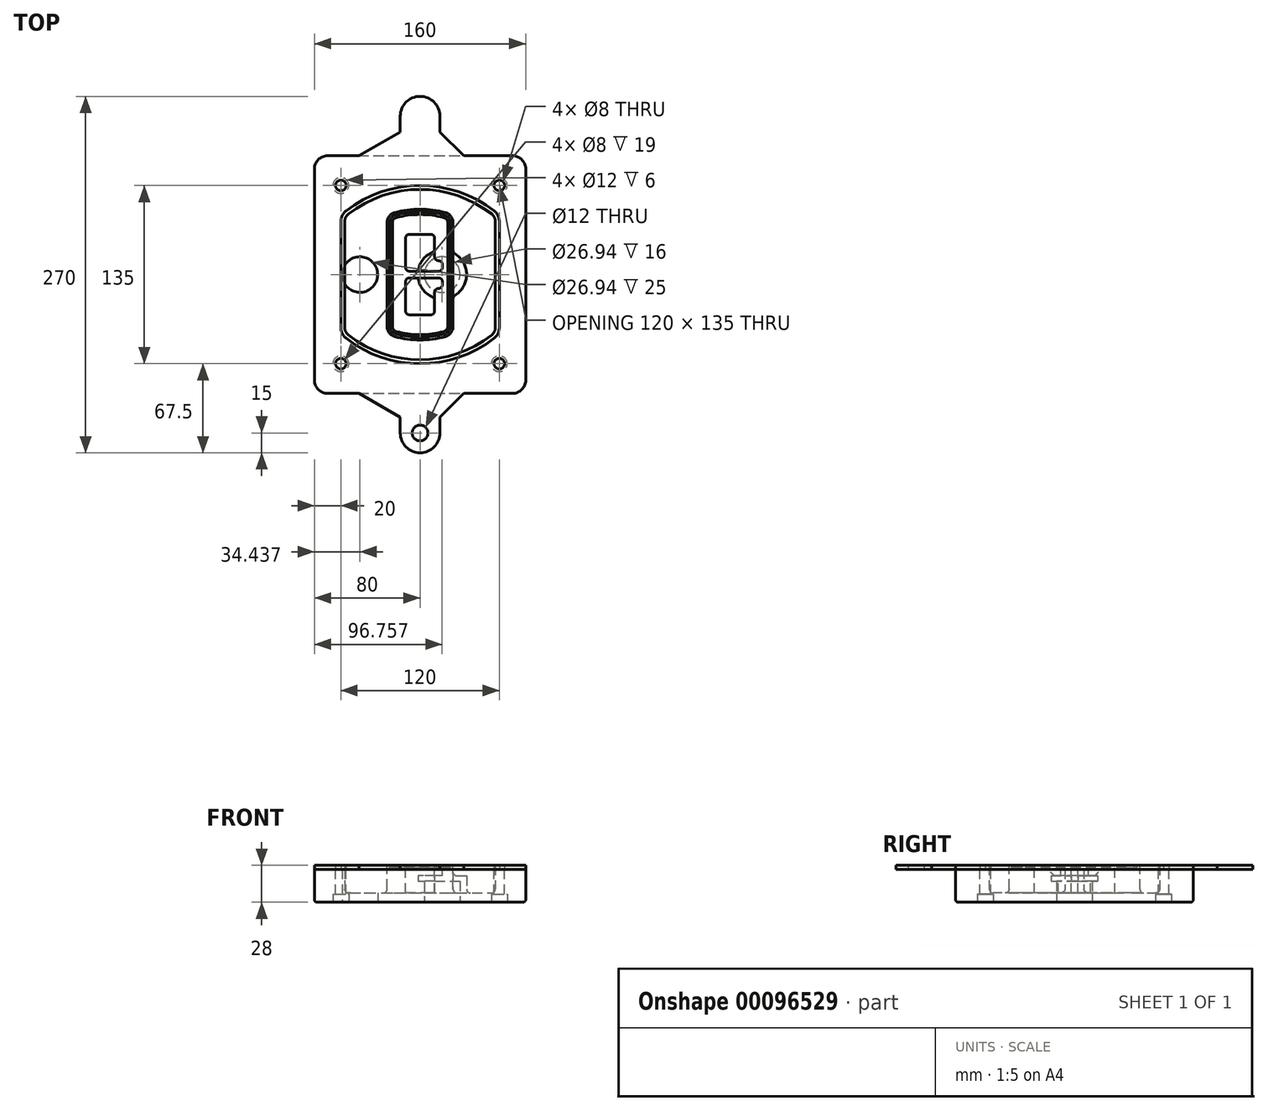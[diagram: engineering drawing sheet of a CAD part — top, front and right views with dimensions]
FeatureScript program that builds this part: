
annotation { "Feature Type Name" : "Feature", "Feature Type Description" : "" }
export const myFeature = defineFeature(function(context is Context, id is Id, definition is map)
    precondition{}
    {
        {
            var Q0;
            Q0=qCreatedBy(makeId("Top.planeOp"),FACE);
            var sketch = newSketch(context, id + "F0", { "sketchPlane" : qUnion([Q0])});
            skPoint(sketch, "E0.rect.middle", {"position": v(0, 0) * mm});
            skLineSegment(sketch, "E1.bottom", {"start": v(-70, -90) * mm, "end": v(70, -90) * mm});
            skLineSegment(sketch, "E1.top", {"start": v(-70, 90) * mm, "end": v(70, 90) * mm});
            skLineSegment(sketch, "E1.left", {"start": v(-80, -80) * mm, "end": v(-80, 80) * mm});
            skLineSegment(sketch, "E1.right", {"start": v(80, -80) * mm, "end": v(80, 80) * mm});
            skLineSegment(sketch, "E2", {"start": v(-80, 90) * mm, "end": v(80, -90) * mm, "construction": true});
            skLineSegment(sketch, "E3", {"start": v(80, 90) * mm, "end": v(-80, -90) * mm, "construction": true});
            skCircle(sketch, "E4", {"center": v(-60, 67.5) * mm, "radius": 4 * mm});
            skCircle(sketch, "E5", {"center": v(60, 67.5) * mm, "radius": 4 * mm});
            skCircle(sketch, "E6", {"center": v(60, -67.5) * mm, "radius": 4 * mm});
            skCircle(sketch, "E7", {"center": v(-60, -67.5) * mm, "radius": 4 * mm});
            skLineSegment(sketch, "E8", {"start": v(-60, 67.5) * mm, "end": v(60, 67.5) * mm, "construction": true});
            skLineSegment(sketch, "E9", {"start": v(60, 67.5) * mm, "end": v(60, -67.5) * mm, "construction": true});
            skLineSegment(sketch, "E10", {"start": v(60, -67.5) * mm, "end": v(-60, -67.5) * mm, "construction": true});
            skLineSegment(sketch, "E11", {"start": v(-60, -67.5) * mm, "end": v(-60, 67.5) * mm, "construction": true});
            skLineSegment(sketch, "E12", {"start": v(-60, 40.3) * mm, "end": v(-60, -40.3) * mm});
            skLineSegment(sketch, "E13", {"start": v(60, 40.3) * mm, "end": v(60, -40.3) * mm});
            skArc(sketch, "E14", {"start": v(56.15, 48.18) * mm, "mid": v(0, 67.5) * mm, "end": v(-56.15, 48.18) * mm});
            skArc(sketch, "E15", {"start": v(-56.15, -48.18) * mm, "mid": v(0, -67.5) * mm, "end": v(56.15, -48.18) * mm});
            skLineSegment(sketch, "E16", {"start": v(-60, 0) * mm, "end": v(60, 0) * mm, "construction": true});
            skPoint(sketch, "E17.visualSharp", {"position": v(-60, -45) * mm});
            skArc(sketch, "E17.filletArc", {"start": v(-60, -40.3) * mm, "mid": v(-58.99, -44.68) * mm, "end": v(-56.15, -48.18) * mm});
            skPoint(sketch, "E18.visualSharp", {"position": v(-60, 45) * mm});
            skArc(sketch, "E18.filletArc", {"start": v(-56.15, 48.18) * mm, "mid": v(-58.99, 44.68) * mm, "end": v(-60, 40.3) * mm});
            skPoint(sketch, "E19.visualSharp", {"position": v(60, 45) * mm});
            skArc(sketch, "E19.filletArc", {"start": v(60, 40.3) * mm, "mid": v(58.99, 44.68) * mm, "end": v(56.15, 48.18) * mm});
            skPoint(sketch, "E20.visualSharp", {"position": v(60, -45) * mm});
            skArc(sketch, "E20.filletArc", {"start": v(56.15, -48.18) * mm, "mid": v(58.99, -44.68) * mm, "end": v(60, -40.3) * mm});
            skPoint(sketch, "E21.visualSharp", {"position": v(-80, 90) * mm});
            skArc(sketch, "E21.filletArc", {"start": v(-70, 90) * mm, "mid": v(-77.07, 87.07) * mm, "end": v(-80, 80) * mm});
            skPoint(sketch, "E22.visualSharp", {"position": v(80, 90) * mm});
            skArc(sketch, "E22.filletArc", {"start": v(80, 80) * mm, "mid": v(77.07, 87.07) * mm, "end": v(70, 90) * mm});
            skPoint(sketch, "E23.visualSharp", {"position": v(80, -90) * mm});
            skArc(sketch, "E23.filletArc", {"start": v(70, -90) * mm, "mid": v(77.07, -87.07) * mm, "end": v(80, -80) * mm});
            skPoint(sketch, "E24.visualSharp", {"position": v(-80, -90) * mm});
            skArc(sketch, "E24.filletArc", {"start": v(-80, -80) * mm, "mid": v(-77.07, -87.07) * mm, "end": v(-70, -90) * mm});
            skArc(sketch, "E25.0", {"start": v(57, 40.3) * mm, "mid": v(56.3, 43.36) * mm, "end": v(54.3, 45.81) * mm});
            skLineSegment(sketch, "E25.1", {"start": v(57, 40.3) * mm, "end": v(57, -40.3) * mm});
            skArc(sketch, "E25.2", {"start": v(54.3, -45.81) * mm, "mid": v(56.3, -43.36) * mm, "end": v(57, -40.3) * mm});
            skArc(sketch, "E25.3", {"start": v(-54.3, -45.81) * mm, "mid": v(0, -64.5) * mm, "end": v(54.3, -45.81) * mm});
            skArc(sketch, "E25.4", {"start": v(-57, -40.3) * mm, "mid": v(-56.3, -43.36) * mm, "end": v(-54.3, -45.81) * mm});
            skArc(sketch, "E25.5", {"start": v(54.3, 45.81) * mm, "mid": v(0, 64.5) * mm, "end": v(-54.3, 45.81) * mm});
            skLineSegment(sketch, "E25.6", {"start": v(-57, 40.3) * mm, "end": v(-57, -40.3) * mm});
            skArc(sketch, "E25.7", {"start": v(-54.3, 45.81) * mm, "mid": v(-56.3, 43.36) * mm, "end": v(-57, 40.3) * mm});
            skArc(sketch, "E26.0", {"start": v(-58.62, 51.33) * mm, "mid": v(-62.58, 46.43) * mm, "end": v(-64, 40.3) * mm});
            skArc(sketch, "E26.1", {"start": v(58.62, 51.33) * mm, "mid": v(0, 71.5) * mm, "end": v(-58.62, 51.33) * mm});
            skArc(sketch, "E26.2", {"start": v(64, 40.3) * mm, "mid": v(62.58, 46.43) * mm, "end": v(58.62, 51.33) * mm});
            skLineSegment(sketch, "E26.3", {"start": v(64, 40.3) * mm, "end": v(64, -40.3) * mm});
            skArc(sketch, "E26.4", {"start": v(58.62, -51.33) * mm, "mid": v(62.58, -46.43) * mm, "end": v(64, -40.3) * mm});
            skLineSegment(sketch, "E26.5", {"start": v(-64, 40.3) * mm, "end": v(-64, -40.3) * mm});
            skArc(sketch, "E26.6", {"start": v(-58.62, -51.33) * mm, "mid": v(0, -71.5) * mm, "end": v(58.62, -51.33) * mm});
            skArc(sketch, "E26.7", {"start": v(-64, -40.3) * mm, "mid": v(-62.58, -46.43) * mm, "end": v(-58.62, -51.33) * mm});
            skSolve(sketch);
        }
        {
            var Q0;
            Q0=makeQuery(id+"F0.imprint","IMPRINT",FACE,{"disambiguationData":[TD([[makeQuery(id+"F0.imprint","IMPRINT",EDGE,{"derivedFrom":sQuery(id+"F0.wireOp",EDGE,"E1.bottom")}),1.0]])]});
            var Q1;
            Q1=makeQuery(id+"F0.imprint","IMPRINT",FACE,{"disambiguationData":[TD([[makeQuery(id+"F0.imprint","IMPRINT",EDGE,{"derivedFrom":sQuery(id+"F0.wireOp",EDGE,"E12")}),1.0]])]});
            var Q2;
            Q2=makeQuery(id+"F0.imprint","IMPRINT",FACE,{"disambiguationData":[TD([[makeQuery(id+"F0.imprint","IMPRINT",EDGE,{"derivedFrom":sQuery(id+"F0.wireOp",EDGE,"E25.0")}),1.0]])]});
            var Q3;
            Q3=makeQuery(id+"F0.imprint","IMPRINT",FACE,{"disambiguationData":[TD([[makeQuery(id+"F0.imprint","IMPRINT",EDGE,{"derivedFrom":sQuery(id+"F0.wireOp",EDGE,"E12")}),-1.0]])]});
            extrude(context, id + "F1", {"entities" : qUnion([Q0, Q1, Q2, Q3]), "oppositeDirection" : true, "depth" : 25 * mm});
        }
        {
            var Q0;
            Q0=makeQuery(id+"F0.imprint","IMPRINT",FACE,{"disambiguationData":[TD([[makeQuery(id+"F0.imprint","IMPRINT",EDGE,{"derivedFrom":sQuery(id+"F0.wireOp",EDGE,"E12")}),1.0]])]});
            extrude(context, id + "F2", {"entities" : qUnion([Q0]), "operationType" : NewBodyOperationType.ADD, "depth" : 3 * mm});
        }
        {
            var Q0;
            Q0=makeQuery(id+"F0.imprint","IMPRINT",FACE,{"disambiguationData":[TD([[makeQuery(id+"F0.imprint","IMPRINT",EDGE,{"derivedFrom":sQuery(id+"F0.wireOp",EDGE,"E25.0")}),1.0]])]});
            extrude(context, id + "F3", {"entities" : qUnion([Q0]), "operationType" : NewBodyOperationType.REMOVE, "oppositeDirection" : true, "depth" : 18 * mm});
        }
        {
            var Q0;
            Q0=makeQuery(id+"F2.opExtrude","CAP_FACE",FACE,{"disambiguationData":[OSD([sQuery(id+"F0.wireOp",EDGE,"E12"),sQuery(id+"F0.wireOp",EDGE,"E13"),sQuery(id+"F0.wireOp",EDGE,"E14"),sQuery(id+"F0.wireOp",EDGE,"E15"),sQuery(id+"F0.wireOp",EDGE,"E17.filletArc"),sQuery(id+"F0.wireOp",EDGE,"E18.filletArc"),sQuery(id+"F0.wireOp",EDGE,"E19.filletArc"),sQuery(id+"F0.wireOp",EDGE,"E20.filletArc"),sQuery(id+"F0.wireOp",EDGE,"E25.0"),sQuery(id+"F0.wireOp",EDGE,"E25.1"),sQuery(id+"F0.wireOp",EDGE,"E25.2"),sQuery(id+"F0.wireOp",EDGE,"E25.3"),sQuery(id+"F0.wireOp",EDGE,"E25.4"),sQuery(id+"F0.wireOp",EDGE,"E25.5"),sQuery(id+"F0.wireOp",EDGE,"E25.6"),sQuery(id+"F0.wireOp",EDGE,"E25.7")])],"isStart":false});
            var sketch = newSketch(context, id + "F4", { "sketchPlane" : qUnion([Q0])});
            skArc(sketch, "E27.0", {"start": v(-19.08, -46.97) * mm, "mid": v(0, -49.5) * mm, "end": v(19.08, -46.97) * mm});
            skArc(sketch, "E28.0", {"start": v(19.08, 46.97) * mm, "mid": v(0, 49.5) * mm, "end": v(-19.08, 46.97) * mm});
            skLineSegment(sketch, "E29", {"start": v(-25, 39.25) * mm, "end": v(-25, -39.25) * mm});
            skLineSegment(sketch, "E30", {"start": v(25, 39.25) * mm, "end": v(25, -39.25) * mm});
            skLineSegment(sketch, "E31", {"start": v(-25, 45.1) * mm, "end": v(25, 45.1) * mm, "construction": true});
            skLineSegment(sketch, "E32", {"start": v(-25, -45.1) * mm, "end": v(25, -45.1) * mm, "construction": true});
            skPoint(sketch, "E33.visualSharp", {"position": v(-25, 45.1) * mm});
            skArc(sketch, "E33.filletArc", {"start": v(-19.08, 46.97) * mm, "mid": v(-23.35, 44.11) * mm, "end": v(-25, 39.25) * mm});
            skPoint(sketch, "E34.visualSharp", {"position": v(25, 45.1) * mm});
            skArc(sketch, "E34.filletArc", {"start": v(25, 39.25) * mm, "mid": v(23.35, 44.11) * mm, "end": v(19.08, 46.97) * mm});
            skPoint(sketch, "E35.visualSharp", {"position": v(25, -45.1) * mm});
            skArc(sketch, "E35.filletArc", {"start": v(19.08, -46.97) * mm, "mid": v(23.35, -44.11) * mm, "end": v(25, -39.25) * mm});
            skPoint(sketch, "E36.visualSharp", {"position": v(-25, -45.1) * mm});
            skArc(sketch, "E36.filletArc", {"start": v(-25, -39.25) * mm, "mid": v(-23.35, -44.11) * mm, "end": v(-19.08, -46.97) * mm});
            skArc(sketch, "E37.0", {"start": v(54.3, 45.81) * mm, "mid": v(0, 64.5) * mm, "end": v(-54.3, 45.81) * mm});
            skArc(sketch, "E37.1", {"start": v(-54.3, 45.81) * mm, "mid": v(-56.3, 43.36) * mm, "end": v(-57, 40.3) * mm});
            skLineSegment(sketch, "E37.2", {"start": v(-57, 40.3) * mm, "end": v(-57, -40.3) * mm});
            skArc(sketch, "E37.3", {"start": v(-57, -40.3) * mm, "mid": v(-56.3, -43.36) * mm, "end": v(-54.3, -45.81) * mm});
            skArc(sketch, "E37.4", {"start": v(-54.3, -45.81) * mm, "mid": v(0, -64.5) * mm, "end": v(54.3, -45.81) * mm});
            skArc(sketch, "E37.5", {"start": v(54.3, -45.81) * mm, "mid": v(56.3, -43.36) * mm, "end": v(57, -40.3) * mm});
            skLineSegment(sketch, "E37.6", {"start": v(57, 40.3) * mm, "end": v(57, -40.3) * mm});
            skArc(sketch, "E37.7", {"start": v(57, 40.3) * mm, "mid": v(56.3, 43.36) * mm, "end": v(54.3, 45.81) * mm});
            skLineSegment(sketch, "E38.0", {"start": v(23, 39.25) * mm, "end": v(23, -39.25) * mm});
            skArc(sketch, "E38.1", {"start": v(18.56, -45.04) * mm, "mid": v(21.76, -42.9) * mm, "end": v(23, -39.25) * mm});
            skArc(sketch, "E38.2", {"start": v(-18.56, -45.04) * mm, "mid": v(0, -47.5) * mm, "end": v(18.56, -45.04) * mm});
            skArc(sketch, "E38.3", {"start": v(-23, -39.25) * mm, "mid": v(-21.76, -42.9) * mm, "end": v(-18.56, -45.04) * mm});
            skLineSegment(sketch, "E38.4", {"start": v(-23, 39.25) * mm, "end": v(-23, -39.25) * mm});
            skArc(sketch, "E38.5", {"start": v(23, 39.25) * mm, "mid": v(21.76, 42.9) * mm, "end": v(18.56, 45.04) * mm});
            skArc(sketch, "E38.6", {"start": v(-18.56, 45.04) * mm, "mid": v(-21.76, 42.9) * mm, "end": v(-23, 39.25) * mm});
            skArc(sketch, "E38.7", {"start": v(18.56, 45.04) * mm, "mid": v(0, 47.5) * mm, "end": v(-18.56, 45.04) * mm});
            skArc(sketch, "E39.0", {"start": v(21, 39.25) * mm, "mid": v(20.18, 41.68) * mm, "end": v(18.04, 43.1) * mm});
            skLineSegment(sketch, "E39.1", {"start": v(21, 39.25) * mm, "end": v(21, -39.25) * mm});
            skArc(sketch, "E39.2", {"start": v(18.04, -43.1) * mm, "mid": v(20.18, -41.68) * mm, "end": v(21, -39.25) * mm});
            skArc(sketch, "E39.3", {"start": v(-18.04, -43.1) * mm, "mid": v(0, -45.5) * mm, "end": v(18.04, -43.1) * mm});
            skArc(sketch, "E39.4", {"start": v(-21, -39.25) * mm, "mid": v(-20.18, -41.68) * mm, "end": v(-18.04, -43.1) * mm});
            skArc(sketch, "E39.5", {"start": v(18.04, 43.1) * mm, "mid": v(0, 45.5) * mm, "end": v(-18.04, 43.1) * mm});
            skLineSegment(sketch, "E39.6", {"start": v(-21, 39.25) * mm, "end": v(-21, -39.25) * mm});
            skArc(sketch, "E39.7", {"start": v(-18.04, 43.1) * mm, "mid": v(-20.18, 41.68) * mm, "end": v(-21, 39.25) * mm});
            skLineSegment(sketch, "E40", {"start": v(-25, 0) * mm, "end": v(25, 0) * mm, "construction": true});
            skLineSegment(sketch, "E41", {"start": v(-11, 5.5) * mm, "end": v(-11, 27.5) * mm});
            skLineSegment(sketch, "E42", {"start": v(-8, 30.5) * mm, "end": v(8, 30.5) * mm});
            skLineSegment(sketch, "E43", {"start": v(11, 27.5) * mm, "end": v(11, 13.5) * mm});
            skLineSegment(sketch, "E44", {"start": v(14, 10.5) * mm, "end": v(14, 10.5) * mm});
            skLineSegment(sketch, "E45", {"start": v(17, 7.5) * mm, "end": v(17, 5.5) * mm});
            skLineSegment(sketch, "E46", {"start": v(14, 2.5) * mm, "end": v(-8, 2.5) * mm});
            skPoint(sketch, "E47.visualSharp", {"position": v(-11, 30.5) * mm});
            skArc(sketch, "E47.filletArc", {"start": v(-8, 30.5) * mm, "mid": v(-10.12, 29.62) * mm, "end": v(-11, 27.5) * mm});
            skPoint(sketch, "E48.visualSharp", {"position": v(11, 30.5) * mm});
            skArc(sketch, "E48.filletArc", {"start": v(11, 27.5) * mm, "mid": v(10.12, 29.62) * mm, "end": v(8, 30.5) * mm});
            skPoint(sketch, "E49.visualSharp", {"position": v(11, 10.5) * mm});
            skArc(sketch, "E49.filletArc", {"start": v(11, 13.5) * mm, "mid": v(11.88, 11.38) * mm, "end": v(14, 10.5) * mm});
            skPoint(sketch, "E50.visualSharp", {"position": v(17, 10.5) * mm});
            skArc(sketch, "E50.filletArc", {"start": v(17, 7.5) * mm, "mid": v(16.12, 9.62) * mm, "end": v(14, 10.5) * mm});
            skPoint(sketch, "E51.visualSharp", {"position": v(17, 2.5) * mm});
            skArc(sketch, "E51.filletArc", {"start": v(14, 2.5) * mm, "mid": v(16.12, 3.38) * mm, "end": v(17, 5.5) * mm});
            skPoint(sketch, "E52.visualSharp", {"position": v(-11, 2.5) * mm});
            skArc(sketch, "E52.filletArc", {"start": v(-11, 5.5) * mm, "mid": v(-10.12, 3.38) * mm, "end": v(-8, 2.5) * mm});
            skLineSegment(sketch, "E53.0.MirrorCS", {"start": v(14, -2.5) * mm, "end": v(-8, -2.5) * mm});
            skArc(sketch, "E54.0.MirrorCS", {"start": v(-11, -5.5) * mm, "mid": v(-10.12, -3.38) * mm, "end": v(-8, -2.5) * mm});
            skLineSegment(sketch, "E55.0.MirrorCS", {"start": v(-11, -5.5) * mm, "end": v(-11, -27.5) * mm});
            skArc(sketch, "E56.0.MirrorCS", {"start": v(-8, -30.5) * mm, "mid": v(-10.12, -29.62) * mm, "end": v(-11, -27.5) * mm});
            skLineSegment(sketch, "E57.0.MirrorCS", {"start": v(-8, -30.5) * mm, "end": v(8, -30.5) * mm});
            skArc(sketch, "E58.0.MirrorCS", {"start": v(11, -27.5) * mm, "mid": v(10.12, -29.62) * mm, "end": v(8, -30.5) * mm});
            skLineSegment(sketch, "E59.0.MirrorCS", {"start": v(11, -27.5) * mm, "end": v(11, -13.5) * mm});
            skArc(sketch, "E60.0.MirrorCS", {"start": v(11, -13.5) * mm, "mid": v(11.88, -11.38) * mm, "end": v(14, -10.5) * mm});
            skArc(sketch, "E61.0.MirrorCS", {"start": v(17, -7.5) * mm, "mid": v(16.12, -9.62) * mm, "end": v(14, -10.5) * mm});
            skLineSegment(sketch, "E62.0.MirrorCS", {"start": v(17, -7.5) * mm, "end": v(17, -5.5) * mm});
            skArc(sketch, "E63.0.MirrorCS", {"start": v(14, -2.5) * mm, "mid": v(16.12, -3.38) * mm, "end": v(17, -5.5) * mm});
            skSolve(sketch);
        }
        {
            var Q0;
            Q0=makeQuery(id+"F4.imprint","IMPRINT",FACE,{"disambiguationData":[TD([[makeQuery(id+"F4.imprint","IMPRINT",EDGE,{"derivedFrom":sQuery(id+"F4.wireOp",EDGE,"E27.0")}),1.0]])]});
            var Q1;
            Q1=makeQuery(id+"F4.imprint","IMPRINT",FACE,{"disambiguationData":[TD([[makeQuery(id+"F4.imprint","IMPRINT",EDGE,{"derivedFrom":sQuery(id+"F4.wireOp",EDGE,"E38.0")}),-1.0]])]});
            var Q2;
            Q2=makeQuery(id+"F4.imprint","IMPRINT",FACE,{"disambiguationData":[TD([[makeQuery(id+"F4.imprint","IMPRINT",EDGE,{"derivedFrom":sQuery(id+"F4.wireOp",EDGE,"E39.0")}),1.0]])]});
            extrude(context, id + "F5", {"entities" : qUnion([Q0, Q1, Q2]), "operationType" : NewBodyOperationType.ADD, "endBound" : BoundingType.UP_TO_NEXT, "oppositeDirection" : true, "depth" : 25 * mm});
        }
        {
            var Q0;
            Q0=makeQuery(id+"F4.imprint","IMPRINT",FACE,{"disambiguationData":[TD([[makeQuery(id+"F4.imprint","IMPRINT",EDGE,{"derivedFrom":sQuery(id+"F4.wireOp",EDGE,"E38.0")}),-1.0]])]});
            extrude(context, id + "F6", {"entities" : qUnion([Q0]), "operationType" : NewBodyOperationType.REMOVE, "oppositeDirection" : true, "depth" : 2 * mm});
        }
        {
            var Q0;
            Q0=makeQuery(id+"F1.opExtrude","CAP_FACE",FACE,{"disambiguationData":[OSD([sQuery(id+"F0.wireOp",EDGE,"E1.bottom"),sQuery(id+"F0.wireOp",EDGE,"E1.top"),sQuery(id+"F0.wireOp",EDGE,"E1.left"),sQuery(id+"F0.wireOp",EDGE,"E1.right"),sQuery(id+"F0.wireOp",EDGE,"E4"),sQuery(id+"F0.wireOp",EDGE,"E5"),sQuery(id+"F0.wireOp",EDGE,"E6"),sQuery(id+"F0.wireOp",EDGE,"E7"),sQuery(id+"F0.wireOp",EDGE,"E21.filletArc"),sQuery(id+"F0.wireOp",EDGE,"E22.filletArc"),sQuery(id+"F0.wireOp",EDGE,"E23.filletArc"),sQuery(id+"F0.wireOp",EDGE,"E24.filletArc")])],"isStart":false});
            var sketch = newSketch(context, id + "F7", { "sketchPlane" : qUnion([Q0])});
            skCircle(sketch, "E64", {"center": v(16.76, 0) * mm, "radius": 13.47 * mm});
            skCircle(sketch, "E65", {"center": v(-45.56, 0) * mm, "radius": 13.47 * mm});
            skLineSegment(sketch, "E66", {"start": v(80, 0) * mm, "end": v(-80, 0) * mm});
            skCircle(sketch, "E67", {"center": v(16.76, 0) * mm, "radius": 18.47 * mm});
            skCircle(sketch, "E68", {"center": v(60, -67.5) * mm, "radius": 6 * mm});
            skCircle(sketch, "E69", {"center": v(-60, -67.5) * mm, "radius": 6 * mm});
            skCircle(sketch, "E70", {"center": v(-60, 67.5) * mm, "radius": 6 * mm});
            skCircle(sketch, "E71", {"center": v(60, 67.5) * mm, "radius": 6 * mm});
            skSolve(sketch);
        }
        {
            var Q0;
            {var subQ1=sQuery(id+"F7.wireOp",EDGE,"E66");var subQ4=sQuery(id+"F7.wireOp",EDGE,"E64");var subQ6=makeQuery(id+"F7.imprint","INTERSECT",VERTEX,{"disambiguationData":[OD(0.0)],"derivedFrom":[subQ4,subQ1]});Q0=makeQuery(id+"F7.imprint","IMPRINT",FACE,{"disambiguationData":[TD([[makeQuery(id+"F7.imprint","IMPRINT",EDGE,{"disambiguationData":[TD([[subQ6,-1.0]])],"derivedFrom":subQ4}),-1.0]])]});}
            var Q1;
            {var subQ0=sQuery(id+"F7.wireOp",EDGE,"E66");var subQ1=sQuery(id+"F7.wireOp",EDGE,"E64");var subQ3=makeQuery(id+"F7.imprint","INTERSECT",VERTEX,{"disambiguationData":[OD(0.0)],"derivedFrom":[subQ1,subQ0]});Q1=makeQuery(id+"F7.imprint","IMPRINT",FACE,{"disambiguationData":[TD([[makeQuery(id+"F7.imprint","IMPRINT",EDGE,{"disambiguationData":[TD([[subQ3,-1.0]])],"derivedFrom":subQ1}),1.0]])]});}
            var Q2;
            {var subQ0=sQuery(id+"F7.wireOp",EDGE,"E66");var subQ1=sQuery(id+"F7.wireOp",EDGE,"E64");var subQ3=makeQuery(id+"F7.imprint","INTERSECT",VERTEX,{"disambiguationData":[OD(0.0)],"derivedFrom":[subQ1,subQ0]});Q2=makeQuery(id+"F7.imprint","IMPRINT",FACE,{"disambiguationData":[TD([[makeQuery(id+"F7.imprint","IMPRINT",EDGE,{"disambiguationData":[TD([[subQ3,1.0]])],"derivedFrom":subQ1}),1.0]])]});}
            var Q3;
            {var subQ1=sQuery(id+"F7.wireOp",EDGE,"E66");var subQ4=sQuery(id+"F7.wireOp",EDGE,"E64");var subQ6=makeQuery(id+"F7.imprint","INTERSECT",VERTEX,{"disambiguationData":[OD(0.0)],"derivedFrom":[subQ4,subQ1]});Q3=makeQuery(id+"F7.imprint","IMPRINT",FACE,{"disambiguationData":[TD([[makeQuery(id+"F7.imprint","IMPRINT",EDGE,{"disambiguationData":[TD([[subQ6,1.0]])],"derivedFrom":subQ4}),-1.0]])]});}
            extrude(context, id + "F8", {"entities" : qUnion([Q0, Q1, Q2, Q3]), "operationType" : NewBodyOperationType.ADD, "oppositeDirection" : true, "depth" : 20 * mm});
        }
        {
            var Q0;
            {var subQ0=sQuery(id+"F7.wireOp",EDGE,"E66");var subQ1=sQuery(id+"F7.wireOp",EDGE,"E64");var subQ3=makeQuery(id+"F7.imprint","INTERSECT",VERTEX,{"disambiguationData":[OD(0.0)],"derivedFrom":[subQ1,subQ0]});Q0=makeQuery(id+"F7.imprint","IMPRINT",FACE,{"disambiguationData":[TD([[makeQuery(id+"F7.imprint","IMPRINT",EDGE,{"disambiguationData":[TD([[subQ3,-1.0]])],"derivedFrom":subQ1}),1.0]])]});}
            var Q1;
            {var subQ0=sQuery(id+"F7.wireOp",EDGE,"E66");var subQ1=sQuery(id+"F7.wireOp",EDGE,"E64");var subQ3=makeQuery(id+"F7.imprint","INTERSECT",VERTEX,{"disambiguationData":[OD(0.0)],"derivedFrom":[subQ1,subQ0]});Q1=makeQuery(id+"F7.imprint","IMPRINT",FACE,{"disambiguationData":[TD([[makeQuery(id+"F7.imprint","IMPRINT",EDGE,{"disambiguationData":[TD([[subQ3,1.0]])],"derivedFrom":subQ1}),1.0]])]});}
            extrude(context, id + "F9", {"entities" : qUnion([Q0, Q1]), "operationType" : NewBodyOperationType.REMOVE, "oppositeDirection" : true, "depth" : 16 * mm});
        }
        {
            var Q0;
            {var subQ0=sQuery(id+"F7.wireOp",EDGE,"E66");var subQ1=sQuery(id+"F7.wireOp",EDGE,"E65");var subQ3=makeQuery(id+"F7.imprint","INTERSECT",VERTEX,{"disambiguationData":[OD(0.0)],"derivedFrom":[subQ1,subQ0]});Q0=makeQuery(id+"F7.imprint","IMPRINT",FACE,{"disambiguationData":[TD([[makeQuery(id+"F7.imprint","IMPRINT",EDGE,{"disambiguationData":[TD([[subQ3,-1.0]])],"derivedFrom":subQ1}),1.0]])]});}
            var Q1;
            {var subQ0=sQuery(id+"F7.wireOp",EDGE,"E66");var subQ1=sQuery(id+"F7.wireOp",EDGE,"E65");var subQ3=makeQuery(id+"F7.imprint","INTERSECT",VERTEX,{"disambiguationData":[OD(0.0)],"derivedFrom":[subQ1,subQ0]});Q1=makeQuery(id+"F7.imprint","IMPRINT",FACE,{"disambiguationData":[TD([[makeQuery(id+"F7.imprint","IMPRINT",EDGE,{"disambiguationData":[TD([[subQ3,1.0]])],"derivedFrom":subQ1}),1.0]])]});}
            extrude(context, id + "F10", {"entities" : qUnion([Q0, Q1]), "operationType" : NewBodyOperationType.REMOVE, "oppositeDirection" : true, "depth" : 25 * mm});
        }
        {
            var Q0;
            Q0=makeQuery(id+"F7.imprint","IMPRINT",FACE,{"disambiguationData":[TD([[makeQuery(id+"F7.imprint","IMPRINT",EDGE,{"derivedFrom":sQuery(id+"F7.wireOp",EDGE,"E68")}),1.0]])]});
            var Q1;
            Q1=makeQuery(id+"F7.imprint","IMPRINT",FACE,{"disambiguationData":[TD([[makeQuery(id+"F7.imprint","IMPRINT",EDGE,{"derivedFrom":makeQuery(id+"F1.opExtrude","CAP_EDGE",EDGE,{"disambiguationData":[OSD([sQuery(id+"F0.wireOp",EDGE,"E5")])],"isStart":false})}),-1.0]])]});
            var Q2;
            Q2=makeQuery(id+"F7.imprint","IMPRINT",FACE,{"disambiguationData":[TD([[makeQuery(id+"F7.imprint","IMPRINT",EDGE,{"derivedFrom":sQuery(id+"F7.wireOp",EDGE,"E69")}),1.0]])]});
            var Q3;
            Q3=makeQuery(id+"F7.imprint","IMPRINT",FACE,{"disambiguationData":[TD([[makeQuery(id+"F7.imprint","IMPRINT",EDGE,{"derivedFrom":makeQuery(id+"F1.opExtrude","CAP_EDGE",EDGE,{"disambiguationData":[OSD([sQuery(id+"F0.wireOp",EDGE,"E4")])],"isStart":false})}),-1.0]])]});
            var Q4;
            Q4=makeQuery(id+"F7.imprint","IMPRINT",FACE,{"disambiguationData":[TD([[makeQuery(id+"F7.imprint","IMPRINT",EDGE,{"derivedFrom":sQuery(id+"F7.wireOp",EDGE,"E70")}),1.0]])]});
            var Q5;
            Q5=makeQuery(id+"F7.imprint","IMPRINT",FACE,{"disambiguationData":[TD([[makeQuery(id+"F7.imprint","IMPRINT",EDGE,{"derivedFrom":makeQuery(id+"F1.opExtrude","CAP_EDGE",EDGE,{"disambiguationData":[OSD([sQuery(id+"F0.wireOp",EDGE,"E7")])],"isStart":false})}),-1.0]])]});
            var Q6;
            Q6=makeQuery(id+"F7.imprint","IMPRINT",FACE,{"disambiguationData":[TD([[makeQuery(id+"F7.imprint","IMPRINT",EDGE,{"derivedFrom":sQuery(id+"F7.wireOp",EDGE,"E71")}),1.0]])]});
            var Q7;
            Q7=makeQuery(id+"F7.imprint","IMPRINT",FACE,{"disambiguationData":[TD([[makeQuery(id+"F7.imprint","IMPRINT",EDGE,{"derivedFrom":makeQuery(id+"F1.opExtrude","CAP_EDGE",EDGE,{"disambiguationData":[OSD([sQuery(id+"F0.wireOp",EDGE,"E6")])],"isStart":false})}),-1.0]])]});
            extrude(context, id + "F11", {"entities" : qUnion([Q0, Q1, Q2, Q3, Q4, Q5, Q6, Q7]), "operationType" : NewBodyOperationType.REMOVE, "oppositeDirection" : true, "depth" : 6 * mm});
        }
        {
            var Q0;
            Q0=makeQuery(id+"F9.boolean.opBoolean","COPY",FACE,{"derivedFrom":makeQuery(id+"F9.opExtrude","CAP_FACE",FACE,{"disambiguationData":[OSD([sQuery(id+"F7.wireOp",EDGE,"E64")])],"isStart":false})});
            var sketch = newSketch(context, id + "F12", { "sketchPlane" : qUnion([Q0])});
            skArc(sketch, "E72.0", {"start": v(11, 17.55) * mm, "mid": v(2.57, 11.82) * mm, "end": v(-1.54, 2.5) * mm});
            skArc(sketch, "E72.1", {"start": v(-1.54, -2.5) * mm, "mid": v(2.57, -11.82) * mm, "end": v(11, -17.55) * mm});
            skLineSegment(sketch, "E73", {"start": v(-1.54, -2.5) * mm, "end": v(14, -2.5) * mm});
            skLineSegment(sketch, "E74.0", {"start": v(14, 2.5) * mm, "end": v(-1.54, 2.5) * mm});
            skArc(sketch, "E74.1", {"start": v(14, 2.5) * mm, "mid": v(16.12, 3.38) * mm, "end": v(17, 5.5) * mm});
            skLineSegment(sketch, "E74.2", {"start": v(17, 7.5) * mm, "end": v(17, 5.5) * mm});
            skArc(sketch, "E74.3", {"start": v(17, 7.5) * mm, "mid": v(16.12, 9.62) * mm, "end": v(14, 10.5) * mm});
            skArc(sketch, "E74.4", {"start": v(11, 13.5) * mm, "mid": v(11.88, 11.38) * mm, "end": v(14, 10.5) * mm});
            skLineSegment(sketch, "E74.5", {"start": v(11, 17.55) * mm, "end": v(11, 13.5) * mm});
            skLineSegment(sketch, "E74.7", {"start": v(14, -2.5) * mm, "end": v(-1.54, -2.5) * mm});
            skArc(sketch, "E74.8", {"start": v(14, -2.5) * mm, "mid": v(16.12, -3.38) * mm, "end": v(17, -5.5) * mm});
            skLineSegment(sketch, "E74.9", {"start": v(17, -7.5) * mm, "end": v(17, -5.5) * mm});
            skArc(sketch, "E74.10", {"start": v(17, -7.5) * mm, "mid": v(16.12, -9.62) * mm, "end": v(14, -10.5) * mm});
            skArc(sketch, "E74.11", {"start": v(11, -13.5) * mm, "mid": v(11.88, -11.38) * mm, "end": v(14, -10.5) * mm});
            skLineSegment(sketch, "E74.12", {"start": v(11, -17.55) * mm, "end": v(11, -13.5) * mm});
            skPoint(sketch, "E75.orphan", {"position": v(11, -27.5) * mm});
            skPoint(sketch, "E76.orphan", {"position": v(-8, -2.5) * mm});
            skPoint(sketch, "E77.orphan", {"position": v(-8, 2.5) * mm});
            skPoint(sketch, "E78.orphan", {"position": v(11, 27.5) * mm});
            skSolve(sketch);
        }
        {
            var Q0;
            {var subQ7=sQuery(id+"F12.wireOp",EDGE,"E72.0");var subQ14=sQuery(id+"F12.wireOp",EDGE,"E72.1");var subQ16=sQuery(id+"F12.wireOp",EDGE,"E74.1");var subQ18=sQuery(id+"F12.wireOp",EDGE,"E74.8");Q0=qUnion([makeQuery(id+"F12.imprint","IMPRINT",FACE,{"disambiguationData":[TD([[makeQuery(id+"F12.imprint","IMPRINT",EDGE,{"derivedFrom":subQ7}),1.0]])]}),makeQuery(id+"F12.imprint","IMPRINT",FACE,{"disambiguationData":[TD([[makeQuery(id+"F12.imprint","IMPRINT",EDGE,{"derivedFrom":subQ14}),1.0]])]}),makeQuery(id+"F12.imprint","IMPRINT",FACE,{"disambiguationData":[TD([[makeQuery(id+"F12.imprint","IMPRINT",EDGE,{"derivedFrom":subQ16}),1.0]])]}),makeQuery(id+"F12.imprint","IMPRINT",FACE,{"disambiguationData":[TD([[makeQuery(id+"F12.imprint","IMPRINT",EDGE,{"derivedFrom":subQ18}),-1.0]])]})]);}
            var Q1;
            Q1=makeQuery(id+"F5.boolean.opBoolean","SPLIT",FACE,{"disambiguationData":[TD([makeQuery(id+"F5.opExtrude","SWEPT_FACE",FACE,{"disambiguationData":[OSD([sQuery(id+"F4.wireOp",EDGE,"E41")])]})])],"derivedFrom":makeQuery(id+"F3.boolean.opBoolean","COPY",FACE,{"derivedFrom":makeQuery(id+"F3.opExtrude","CAP_FACE",FACE,{"disambiguationData":[OSD([sQuery(id+"F0.wireOp",EDGE,"E25.0"),sQuery(id+"F0.wireOp",EDGE,"E25.1"),sQuery(id+"F0.wireOp",EDGE,"E25.2"),sQuery(id+"F0.wireOp",EDGE,"E25.3"),sQuery(id+"F0.wireOp",EDGE,"E25.4"),sQuery(id+"F0.wireOp",EDGE,"E25.5"),sQuery(id+"F0.wireOp",EDGE,"E25.6"),sQuery(id+"F0.wireOp",EDGE,"E25.7")])],"isStart":false})})});
            extrude(context, id + "F13", {"entities" : qUnion([Q0]), "operationType" : NewBodyOperationType.REMOVE, "endBound" : BoundingType.UP_TO_SURFACE, "endBoundEntityFace" : qUnion([Q1]), "depth" : 25 * mm});
        }
        {
            var Q0;
            Q0=makeQuery(id+"F3.boolean.opBoolean","COPY",EDGE,{"derivedFrom":makeQuery(id+"F3.opExtrude","CAP_EDGE",EDGE,{"disambiguationData":[OSD([sQuery(id+"F0.wireOp",EDGE,"E25.6")])],"isStart":false})});
            var Q1;
            Q1=makeQuery(id+"F8.boolean.opBoolean","INTERSECT",EDGE,{"derivedFrom":[makeQuery(id+"F5.opExtrude","SWEPT_FACE",FACE,{"disambiguationData":[OSD([sQuery(id+"F4.wireOp",EDGE,"E30")])]}),makeQuery(id+"F8.opExtrude","CAP_FACE",FACE,{"disambiguationData":[OSD([sQuery(id+"F7.wireOp",EDGE,"E67")])],"isStart":false})]});
            var Q2;
            Q2=makeQuery(id+"F8.boolean.opBoolean","INTERSECT",EDGE,{"disambiguationData":[OD(1.0)],"derivedFrom":[makeQuery(id+"F5.opExtrude","SWEPT_FACE",FACE,{"disambiguationData":[OSD([sQuery(id+"F4.wireOp",EDGE,"E30")])]}),makeQuery(id+"F8.opExtrude","SWEPT_FACE",FACE,{"disambiguationData":[OSD([sQuery(id+"F7.wireOp",EDGE,"E67")])]})]});
            var Q3;
            {var subQ0=sQuery(id+"F4.wireOp",EDGE,"E30");Q3=makeQuery(id+"F8.boolean.opBoolean","SPLIT",EDGE,{"disambiguationData":[TD([makeQuery(id+"F5.opExtrude","SWEPT_FACE",FACE,{"disambiguationData":[OSD([sQuery(id+"F4.wireOp",EDGE,"E35.filletArc")])]})])],"derivedFrom":makeQuery(id+"F5.opExtrude","CAP_EDGE",EDGE,{"disambiguationData":[OSD([subQ0])],"isStart":false})});}
            var Q4;
            {var subQ0=sQuery(id+"F0.wireOp",EDGE,"E25.7");var subQ1=sQuery(id+"F0.wireOp",EDGE,"E25.1");var subQ2=sQuery(id+"F0.wireOp",EDGE,"E25.6");var subQ3=sQuery(id+"F0.wireOp",EDGE,"E25.5");var subQ4=sQuery(id+"F0.wireOp",EDGE,"E25.4");var subQ5=sQuery(id+"F0.wireOp",EDGE,"E25.0");var subQ6=sQuery(id+"F0.wireOp",EDGE,"E25.2");var subQ7=sQuery(id+"F0.wireOp",EDGE,"E25.3");Q4=makeQuery(id+"F8.boolean.opBoolean","INTERSECT",EDGE,{"derivedFrom":[makeQuery(id+"F5.boolean.opBoolean","SPLIT",FACE,{"disambiguationData":[TD([makeQuery(id+"F2.opExtrude","SWEPT_FACE",FACE,{"disambiguationData":[OSD([subQ5])]})])],"derivedFrom":makeQuery(id+"F3.boolean.opBoolean","COPY",FACE,{"derivedFrom":makeQuery(id+"F3.opExtrude","CAP_FACE",FACE,{"disambiguationData":[OSD([subQ5,subQ1,subQ6,subQ7,subQ4,subQ3,subQ2,subQ0])],"isStart":false})})}),makeQuery(id+"F8.opExtrude","SWEPT_FACE",FACE,{"disambiguationData":[OSD([sQuery(id+"F7.wireOp",EDGE,"E67")])]})]});}
            var Q5;
            Q5=makeQuery(id+"F8.boolean.opBoolean","INTERSECT",EDGE,{"disambiguationData":[OD(0.0)],"derivedFrom":[makeQuery(id+"F5.opExtrude","SWEPT_FACE",FACE,{"disambiguationData":[OSD([sQuery(id+"F4.wireOp",EDGE,"E30")])]}),makeQuery(id+"F8.opExtrude","SWEPT_FACE",FACE,{"disambiguationData":[OSD([sQuery(id+"F7.wireOp",EDGE,"E67")])]})]});
            fillet(context, id + "F14", {"entities" : qUnion([Q0, Q1, Q2, Q3, Q4, Q5]), "radius" : 3 * mm, "tangentPropagation" : true, "allowEdgeOverflow" : false});
        }
        {
            var Q0;
            Q0=makeQuery(id+"F1.opExtrude","CAP_EDGE",EDGE,{"disambiguationData":[OSD([sQuery(id+"F0.wireOp",EDGE,"E1.bottom")])],"isStart":false});
            fillet(context, id + "F15", {"entities" : qUnion([Q0]), "radius" : 2 * mm, "tangentPropagation" : true, "allowEdgeOverflow" : false});
        }
        {
            var Q0;
            {var subQ0=sQuery(id+"F0.wireOp",EDGE,"E22.filletArc");var subQ1=sQuery(id+"F0.wireOp",EDGE,"E7");var subQ2=sQuery(id+"F0.wireOp",EDGE,"E6");var subQ3=sQuery(id+"F0.wireOp",EDGE,"E5");var subQ4=sQuery(id+"F0.wireOp",EDGE,"E4");var subQ5=sQuery(id+"F0.wireOp",EDGE,"E1.bottom");var subQ6=sQuery(id+"F0.wireOp",EDGE,"E21.filletArc");var subQ7=sQuery(id+"F0.wireOp",EDGE,"E1.top");var subQ8=sQuery(id+"F0.wireOp",EDGE,"E1.left");var subQ9=sQuery(id+"F0.wireOp",EDGE,"E1.right");var subQ10=sQuery(id+"F0.wireOp",EDGE,"E23.filletArc");var subQ11=sQuery(id+"F0.wireOp",EDGE,"E24.filletArc");Q0=makeQuery(id+"F2.boolean.opBoolean","SPLIT",FACE,{"disambiguationData":[TD([makeQuery(id+"F1.opExtrude","SWEPT_FACE",FACE,{"disambiguationData":[OSD([subQ5])]})])],"derivedFrom":makeQuery(id+"F1.opExtrude","CAP_FACE",FACE,{"disambiguationData":[OSD([subQ5,subQ7,subQ8,subQ9,subQ4,subQ3,subQ2,subQ1,subQ6,subQ0,subQ10,subQ11])],"isStart":true})});}
            var sketch = newSketch(context, id + "F16", { "sketchPlane" : qUnion([Q0])});
            skLineSegment(sketch, "E79", {"start": v(0, 90) * mm, "end": v(0, 120) * mm, "construction": true});
            skCircle(sketch, "E80", {"center": v(0, 120) * mm, "radius": 6 * mm});
            skArc(sketch, "E81", {"start": v(-15, 120) * mm, "mid": v(0, 135) * mm, "end": v(15, 120) * mm});
            skLineSegment(sketch, "E82", {"start": v(15, 120) * mm, "end": v(15, 108) * mm});
            skLineSegment(sketch, "E83", {"start": v(-15, 120) * mm, "end": v(-15, 108) * mm});
            skLineSegment(sketch, "E84", {"start": v(15, 108) * mm, "end": v(33, 90) * mm});
            skLineSegment(sketch, "E85", {"start": v(-15, 108) * mm, "end": v(-46.33, 90) * mm});
            skLineSegment(sketch, "E86", {"start": v(-80, 0) * mm, "end": v(80, 0) * mm, "construction": true});
            skLineSegment(sketch, "E87.MirrorCS", {"start": v(15, -108) * mm, "end": v(33, -90) * mm});
            skLineSegment(sketch, "E88.MirrorCS", {"start": v(-15, -108) * mm, "end": v(-46.33, -90) * mm});
            skLineSegment(sketch, "E89.MirrorCS", {"start": v(-15, -120) * mm, "end": v(-15, -108) * mm});
            skLineSegment(sketch, "E90.MirrorCS", {"start": v(15, -120) * mm, "end": v(15, -108) * mm});
            skCircle(sketch, "E91.MirrorC", {"center": v(0, -120) * mm, "radius": 6 * mm});
            skLineSegment(sketch, "E92.MirrorCS", {"start": v(0, -90) * mm, "end": v(0, -120) * mm, "construction": true});
            skArc(sketch, "E93.MirrorCS", {"start": v(-15, -120) * mm, "mid": v(0, -135) * mm, "end": v(15, -120) * mm});
            skSolve(sketch);
        }
        {
            var Q0;
            Q0=makeQuery(id+"F16.imprint","IMPRINT",FACE,{"disambiguationData":[TD([[makeQuery(id+"F16.imprint","IMPRINT",EDGE,{"derivedFrom":sQuery(id+"F16.wireOp",EDGE,"E80")}),1.0]])]});
            var Q1;
            {var subQ0=sQuery(id+"F16.wireOp",EDGE,"E87.MirrorCS");Q1=makeQuery(id+"F16.imprint","IMPRINT",FACE,{"disambiguationData":[TD([[makeQuery(id+"F16.imprint","IMPRINT",EDGE,{"derivedFrom":subQ0}),1.0]])]});}
            var Q2;
            Q2=makeQuery(id+"F16.imprint","IMPRINT",FACE,{"disambiguationData":[TD([[makeQuery(id+"F16.imprint","IMPRINT",EDGE,{"derivedFrom":makeQuery(id+"F1.opExtrude","CAP_EDGE",EDGE,{"disambiguationData":[OSD([sQuery(id+"F0.wireOp",EDGE,"E1.left")])],"isStart":true})}),-1.0]])]});
            var Q3;
            Q3=makeQuery(id+"F16.imprint","IMPRINT",FACE,{"disambiguationData":[TD([[makeQuery(id+"F16.imprint","IMPRINT",EDGE,{"derivedFrom":sQuery(id+"F16.wireOp",EDGE,"E80")}),-1.0]])]});
            var Q4;
            Q4=makeQuery(id+"F2.opExtrude","CAP_FACE",FACE,{"disambiguationData":[OSD([sQuery(id+"F0.wireOp",EDGE,"E12"),sQuery(id+"F0.wireOp",EDGE,"E13"),sQuery(id+"F0.wireOp",EDGE,"E14"),sQuery(id+"F0.wireOp",EDGE,"E15"),sQuery(id+"F0.wireOp",EDGE,"E17.filletArc"),sQuery(id+"F0.wireOp",EDGE,"E18.filletArc"),sQuery(id+"F0.wireOp",EDGE,"E19.filletArc"),sQuery(id+"F0.wireOp",EDGE,"E20.filletArc"),sQuery(id+"F0.wireOp",EDGE,"E25.0"),sQuery(id+"F0.wireOp",EDGE,"E25.1"),sQuery(id+"F0.wireOp",EDGE,"E25.2"),sQuery(id+"F0.wireOp",EDGE,"E25.3"),sQuery(id+"F0.wireOp",EDGE,"E25.4"),sQuery(id+"F0.wireOp",EDGE,"E25.5"),sQuery(id+"F0.wireOp",EDGE,"E25.6"),sQuery(id+"F0.wireOp",EDGE,"E25.7")])],"isStart":false});
            extrude(context, id + "F17", {"entities" : qUnion([Q0, Q1, Q2, Q3]), "endBound" : BoundingType.UP_TO_SURFACE, "endBoundEntityFace" : qUnion([Q4]), "depth" : 25 * mm});
        }
    });
